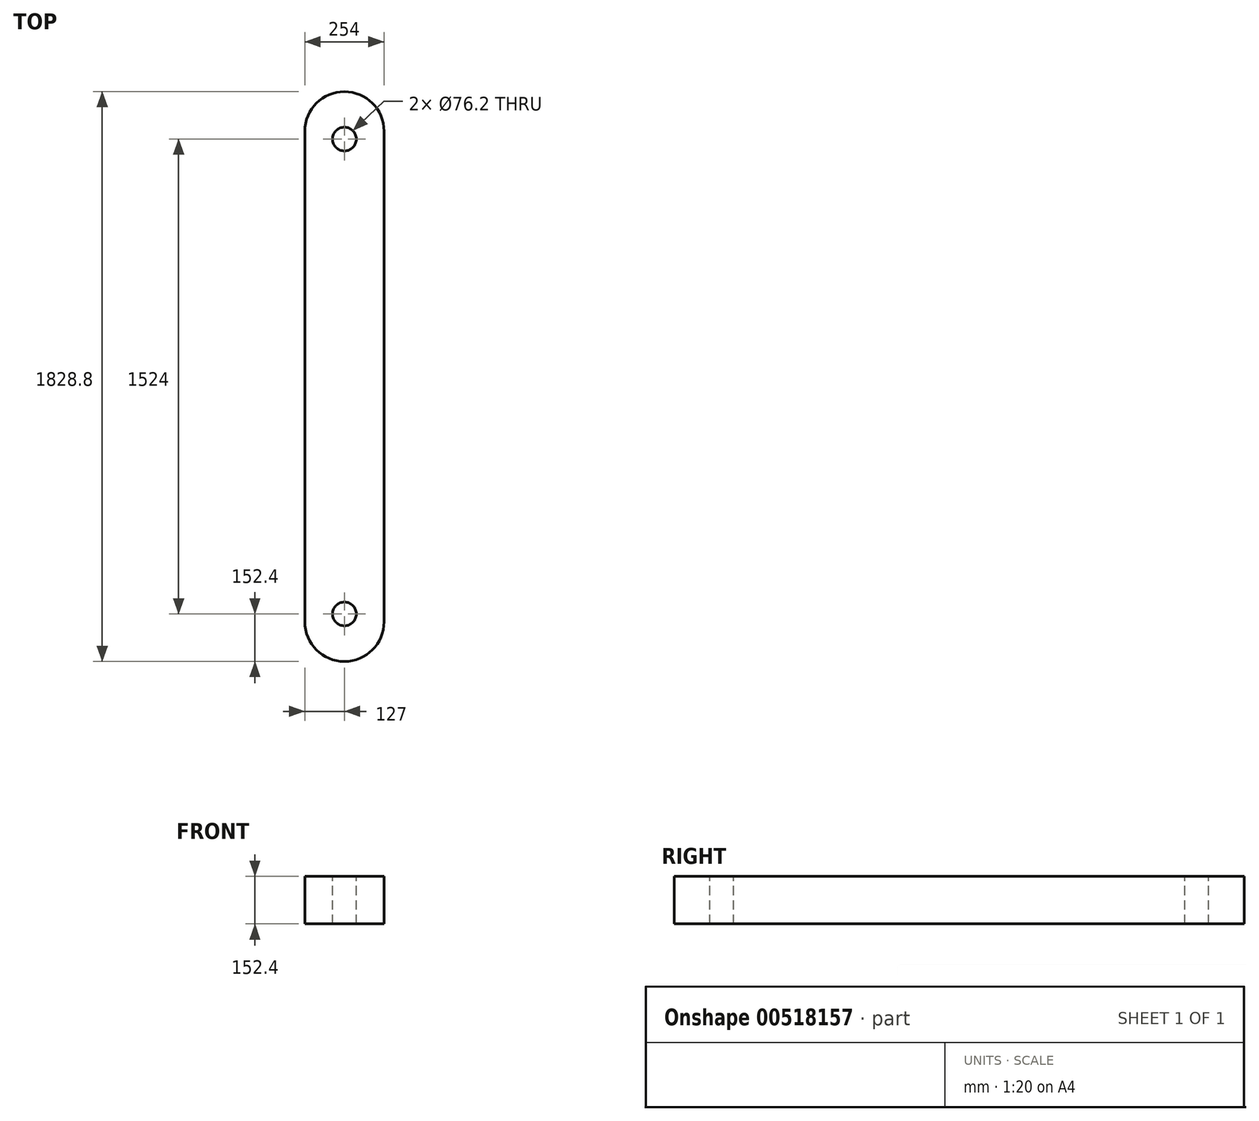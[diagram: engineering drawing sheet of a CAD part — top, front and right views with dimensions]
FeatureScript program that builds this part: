
annotation { "Feature Type Name" : "Feature", "Feature Type Description" : "" }
export const myFeature = defineFeature(function(context is Context, id is Id, definition is map)
    precondition{}
    {
        {
            var Q0;
            Q0=qCreatedBy(makeId("Front.planeOp"),FACE);
            var sketch = newSketch(context, id + "F0", { "sketchPlane" : qUnion([Q0])});
            skLineSegment(sketch, "E0.bottom", {"start": v(-127, -76.2) * mm, "end": v(127, -76.2) * mm});
            skLineSegment(sketch, "E0.top", {"start": v(-127, 76.2) * mm, "end": v(127, 76.2) * mm});
            skLineSegment(sketch, "E0.left", {"start": v(-127, -76.2) * mm, "end": v(-127, 76.2) * mm});
            skLineSegment(sketch, "E0.right", {"start": v(127, -76.2) * mm, "end": v(127, 76.2) * mm});
            skLineSegment(sketch, "E1", {"start": v(0, 76.2) * mm, "end": v(0, -76.2) * mm, "construction": true});
            skLineSegment(sketch, "E2", {"start": v(-127, 0) * mm, "end": v(127, 0) * mm, "construction": true});
            skSolve(sketch);
        }
        {
            var Q0;
            Q0 = qSketchRegion(id + "F0", true);
            extrude(context, id + "F1", {"entities" : qUnion([Q0]), "endBound" : BoundingType.SYMMETRIC, "depth" : 1828.8 * mm, "offsetDistance" : 25.4 * mm});
        }
        {
            var Q0;
            Q0=makeQuery(id+"F1.opExtrude","SWEPT_FACE",FACE,{"disambiguationData":[OSD([sQuery(id+"F0.wireOp",EDGE,"E0.top")])]});
            var sketch = newSketch(context, id + "F2", { "sketchPlane" : qUnion([Q0])});
            skPoint(sketch, "E3", {"position": v(0, 762) * mm});
            skLineSegment(sketch, "E4", {"start": v(-127, 0) * mm, "end": v(0, 0) * mm, "construction": true});
            skPoint(sketch, "E4.endSnap0", {"position": v(127, 0) * mm});
            skPoint(sketch, "E5.MirrorP", {"position": v(0, -762) * mm});
            skPoint(sketch, "E6", {"position": v(-127, 0) * mm});
            skSolve(sketch);
        }
        {
            var Q0;
            Q0=sQuery(id+"F2.wireOp",VERTEX,"E3");
            var Q1;
            Q1=sQuery(id+"F2.wireOp",VERTEX,"E5.MirrorP");
            var Q2;
            Q2=makeQuery(id+"F1.opExtrude","SWEPT_BODY",BODY,{"disambiguationData":[OSD([sQuery(id+"F0.wireOp",EDGE,"E0.bottom"),sQuery(id+"F0.wireOp",EDGE,"E0.top"),sQuery(id+"F0.wireOp",EDGE,"E0.left"),sQuery(id+"F0.wireOp",EDGE,"E0.right")])]});
            hole(context, id + "F3", {"style" : HoleStyle.SIMPLE, "endStyle" : HoleEndStyle.THROUGH, "holeDiameter" : 76.2 * mm, "isTappedThrough" : true, "tappedDepth" : 12.7 * mm, "tapClearance" : 3, "locations" : qUnion([Q0, Q1]), "scope" : qUnion([Q2])});
        }
        {
            var Q0;
            Q0=makeQuery(id+"F1.opExtrude","CAP_EDGE",EDGE,{"disambiguationData":[OSD([sQuery(id+"F0.wireOp",EDGE,"E0.right")])],"isStart":false});
            var Q1;
            Q1=makeQuery(id+"F1.opExtrude","CAP_EDGE",EDGE,{"disambiguationData":[OSD([sQuery(id+"F0.wireOp",EDGE,"E0.left")])],"isStart":false});
            var Q2;
            Q2=makeQuery(id+"F1.opExtrude","CAP_EDGE",EDGE,{"disambiguationData":[OSD([sQuery(id+"F0.wireOp",EDGE,"E0.right")])],"isStart":true});
            var Q3;
            Q3=makeQuery(id+"F1.opExtrude","CAP_EDGE",EDGE,{"disambiguationData":[OSD([sQuery(id+"F0.wireOp",EDGE,"E0.left")])],"isStart":true});
            fillet(context, id + "F4", {"entities" : qUnion([Q0, Q1, Q2, Q3]), "radius" : 127 * mm, "tangentPropagation" : true, "allowEdgeOverflow" : false});
        }
    });
